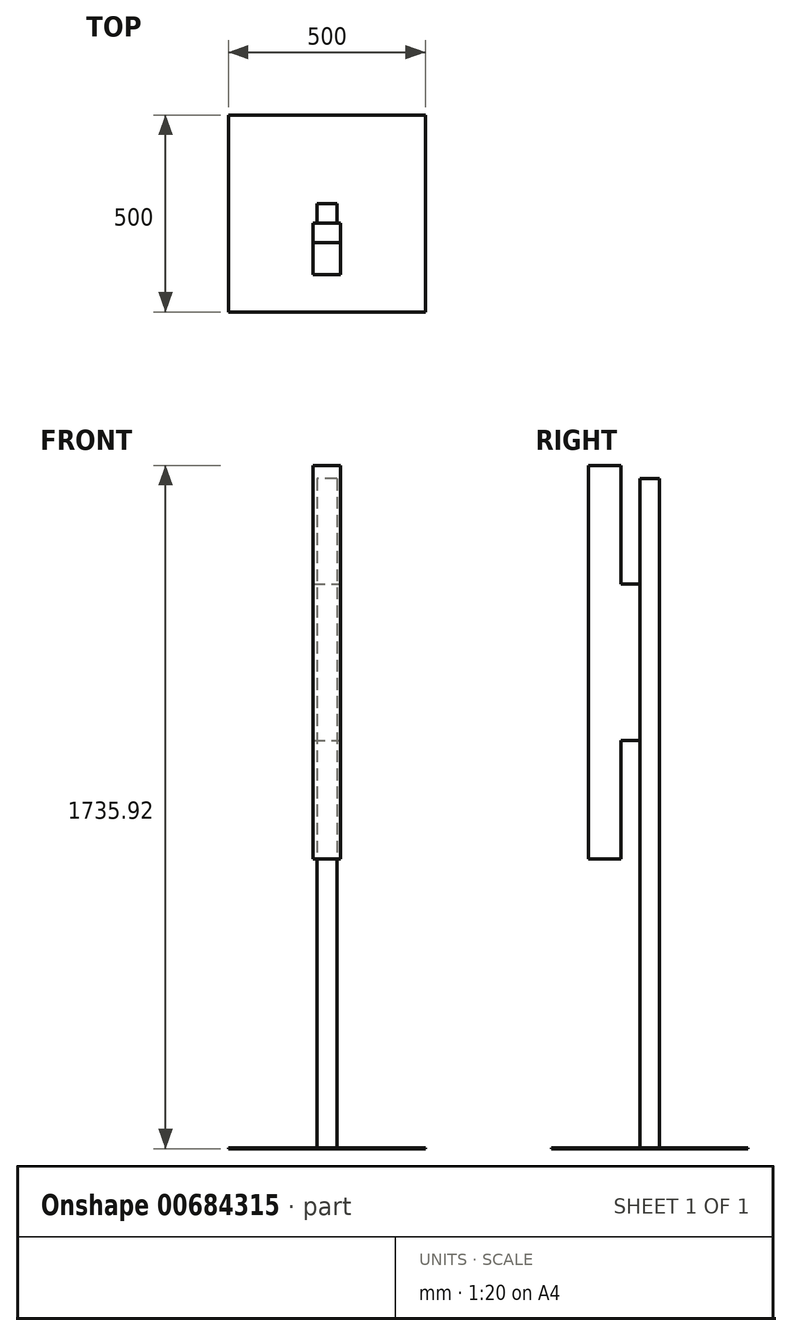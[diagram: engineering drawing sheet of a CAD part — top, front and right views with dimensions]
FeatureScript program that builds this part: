
annotation { "Feature Type Name" : "Feature", "Feature Type Description" : "" }
export const myFeature = defineFeature(function(context is Context, id is Id, definition is map)
    precondition{}
    {
        {
            var Q0;
            Q0=qCreatedBy(makeId("Top.planeOp"),FACE);
            var sketch = newSketch(context, id + "F0", { "sketchPlane" : qUnion([Q0])});
            skLineSegment(sketch, "E0.bottom", {"start": v(-250, -250) * mm, "end": v(250, -250) * mm});
            skLineSegment(sketch, "E0.top", {"start": v(-250, 250) * mm, "end": v(250, 250) * mm});
            skLineSegment(sketch, "E0.left", {"start": v(-250, -250) * mm, "end": v(-250, 250) * mm});
            skLineSegment(sketch, "E0.right", {"start": v(250, -250) * mm, "end": v(250, 250) * mm});
            skPoint(sketch, "E0.middle", {"position": v(0, 0) * mm});
            skSolve(sketch);
        }
        {
            var Q0;
            Q0 = qSketchRegion(id + "F0", true);
            extrude(context, id + "F1", {"entities" : qUnion([Q0]), "depth" : 2 * mm, "offsetDistance" : 25.4 * mm});
        }
        {
            var Q0;
            Q0=makeQuery(id+"F1.opExtrude","CAP_FACE",FACE,{"disambiguationData":[OSD([sQuery(id+"F0.wireOp",EDGE,"E0.bottom"),sQuery(id+"F0.wireOp",EDGE,"E0.top"),sQuery(id+"F0.wireOp",EDGE,"E0.left"),sQuery(id+"F0.wireOp",EDGE,"E0.right")])],"isStart":false});
            var sketch = newSketch(context, id + "F2", { "sketchPlane" : qUnion([Q0])});
            skLineSegment(sketch, "E1.bottom", {"start": v(25, -25) * mm, "end": v(-25, -25) * mm});
            skLineSegment(sketch, "E1.top", {"start": v(25, 25) * mm, "end": v(-25, 25) * mm});
            skLineSegment(sketch, "E1.left", {"start": v(25, -25) * mm, "end": v(25, 25) * mm});
            skLineSegment(sketch, "E1.right", {"start": v(-25, -25) * mm, "end": v(-25, 25) * mm});
            skPoint(sketch, "E1.middle", {"position": v(0, 0) * mm});
            skSolve(sketch);
        }
        {
            var Q0;
            Q0 = qSketchRegion(id + "F2", true);
            extrude(context, id + "F3", {"entities" : qUnion([Q0]), "operationType" : NewBodyOperationType.ADD, "depth" : 1700 * mm, "offsetDistance" : 25 * mm});
        }
        {
            var Q0;
            Q0=makeQuery(id+"F3.opExtrude","SWEPT_FACE",FACE,{"disambiguationData":[OSD([sQuery(id+"F2.wireOp",EDGE,"E1.bottom")])]});
            var sketch = newSketch(context, id + "F4", { "sketchPlane" : qUnion([Q0])});
            skLineSegment(sketch, "E2.bottom", {"start": v(-35, 735.92) * mm, "end": v(35, 735.92) * mm});
            skLineSegment(sketch, "E2.top", {"start": v(-35, 1735.92) * mm, "end": v(35, 1735.92) * mm});
            skLineSegment(sketch, "E2.left", {"start": v(-35, 735.92) * mm, "end": v(-35, 1735.92) * mm});
            skLineSegment(sketch, "E2.right", {"start": v(35, 735.92) * mm, "end": v(35, 1735.92) * mm});
            skPoint(sketch, "E2.middle", {"position": v(0, 1235.92) * mm});
            skSolve(sketch);
        }
        {
            var Q0;
            Q0 = qSketchRegion(id + "F4", true);
            extrude(context, id + "F5", {"entities" : qUnion([Q0]), "depth" : 130 * mm, "offsetDistance" : 25 * mm});
        }
        {
            var Q0;
            Q0=makeQuery(id+"F5.opExtrude","SWEPT_FACE",FACE,{"disambiguationData":[OSD([sQuery(id+"F4.wireOp",EDGE,"E2.right")])]});
            var sketch = newSketch(context, id + "F6", { "sketchPlane" : qUnion([Q0])});
            skLineSegment(sketch, "E3.bottom", {"start": v(-25, 1735.92) * mm, "end": v(-73.52, 1735.92) * mm});
            skLineSegment(sketch, "E3.top", {"start": v(-25, 1435.1) * mm, "end": v(-73.52, 1435.1) * mm});
            skLineSegment(sketch, "E3.left", {"start": v(-25, 1735.92) * mm, "end": v(-25, 1435.1) * mm});
            skLineSegment(sketch, "E3.right", {"start": v(-73.52, 1735.92) * mm, "end": v(-73.52, 1435.1) * mm});
            skLineSegment(sketch, "E4.bottom", {"start": v(-25, 735.92) * mm, "end": v(-73.52, 735.92) * mm});
            skLineSegment(sketch, "E4.top", {"start": v(-25, 1036.74) * mm, "end": v(-73.52, 1036.74) * mm});
            skLineSegment(sketch, "E4.left", {"start": v(-25, 735.92) * mm, "end": v(-25, 1036.74) * mm});
            skLineSegment(sketch, "E4.right", {"start": v(-73.52, 735.92) * mm, "end": v(-73.52, 1036.74) * mm});
            skSolve(sketch);
        }
        {
            var Q0;
            Q0 = qSketchRegion(id + "F6", true);
            extrude(context, id + "F7", {"entities" : qUnion([Q0]), "operationType" : NewBodyOperationType.REMOVE, "endBound" : BoundingType.THROUGH_ALL, "oppositeDirection" : true, "depth" : 25 * mm, "offsetDistance" : 25 * mm});
        }
    });
